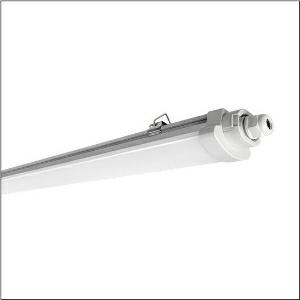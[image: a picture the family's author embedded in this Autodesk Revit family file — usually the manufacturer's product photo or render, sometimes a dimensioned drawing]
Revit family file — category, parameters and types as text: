
# Revit family: monsun_r__41_51fk20mk440a003_a901
name_source: partatom
category: Lighting Fixtures
units: mm (PartAtom-declared; Revit-internal decimal feet)

## family parameters
Cut with Voids When Loaded = No
Host = Face
Light Source = No
Part Type = Normal
Room Calculation Point = No
Round Connector Dimension = Use Diameter
Shared = No

## types (1)
- --- (1 x LED, 4000 lm, 30 W, 4000K)
    Apparent Load = 30 VA
    CIE Flux Codes = 44 74 92 92 100
    Color Rendering = 80
    Color Temperature = 4000K
    Default Elevation = 1800 mm
    Description = Monsun® 41, damp-proof luminaire, primary optical cover: diffuser, of PC, frosted, light emission: direct distribution, primary light characteristic: symmetric, installation type: surface-mounted, suspended mounting, LED, rated luminous flux: 4.000lm, luminous efficacy: 130lm/W, light colour: 840, colour temperature: 4000K, control gear: ON/OFF Multilumen, with terminal, 3-pole, through-wiring: 3x 1.5mm², mains connection: 220..240V, AC, 50/60Hz, rated input power: 30W, housing, luminaire housing, of PC, grey, length: 1.200mm, width: 79mm, height: 52mm, end cap, of PC, grey, ceiling mounting element, of stainless steel (V2A), protection rating (complete): IP65, insulation class (complete): insulation class II (safety insulation), certification: CE, UKCA, protection symbol: D, impact resistance: IK08, permissible operating ambient temperature: -20..+35°C, corresponds to IFS (International Featured Standards) requirements for safety and quality in the food industry, contact your sales advisor before using the luminaires in applications with unclear chemical exposure, large temperature fluctuations or condensation-forming humidity, packaging unit: 1 piece
    Height = 54 mm
    Lamp = 1 x LED
    Lamp Light Flux = 4000 lm
    Lamp Power = 30 W
    Lamp count = 1
    Length = 1200 mm
    Luminous efficacy = 133 lm/W
    Manufacturer = Siteco
    ModVariant = No
    Model = 51FK20MK440A003
    Mounting Place = Ceiling
    Mounting Type = Surface mounted
    Number of Poles = 1
    OnlyDefault = Yes
    Power Factor = 1
    Product Name = Monsun® 41
    Product group = damp-proof luminaire
    ProductGroupID = 300
    Protection Class = Protection class II
    Protection Degree = IP 65
    RLX_Detail_Level = 1
    RLX_Emergency_Light_Flux = 0 lm
    RLX_Emergency_Type = 0
    RLX_Emergency_Type_DB = No
    RlxData = <blob elided: 31917 chars, md5=2d1caac0>
    Socket = socket
    Standby Power = 0 W
    System Light Flux = 4000 lm
    System Power = 30 W
    Type Comments = factory setting: luminous flux: 100 % | (HIGH)
    Type Image = l_1007037.jpg
    URL = http://relux.com
    VarID = @adj_174698
    Voltage = 0 V
    Weight = 0.00 kg
    Width = 79 mm

## geometry (parser evidence)
native form markers: Blend x4, Sweep x13
no freeform markers — native parametric forms only
